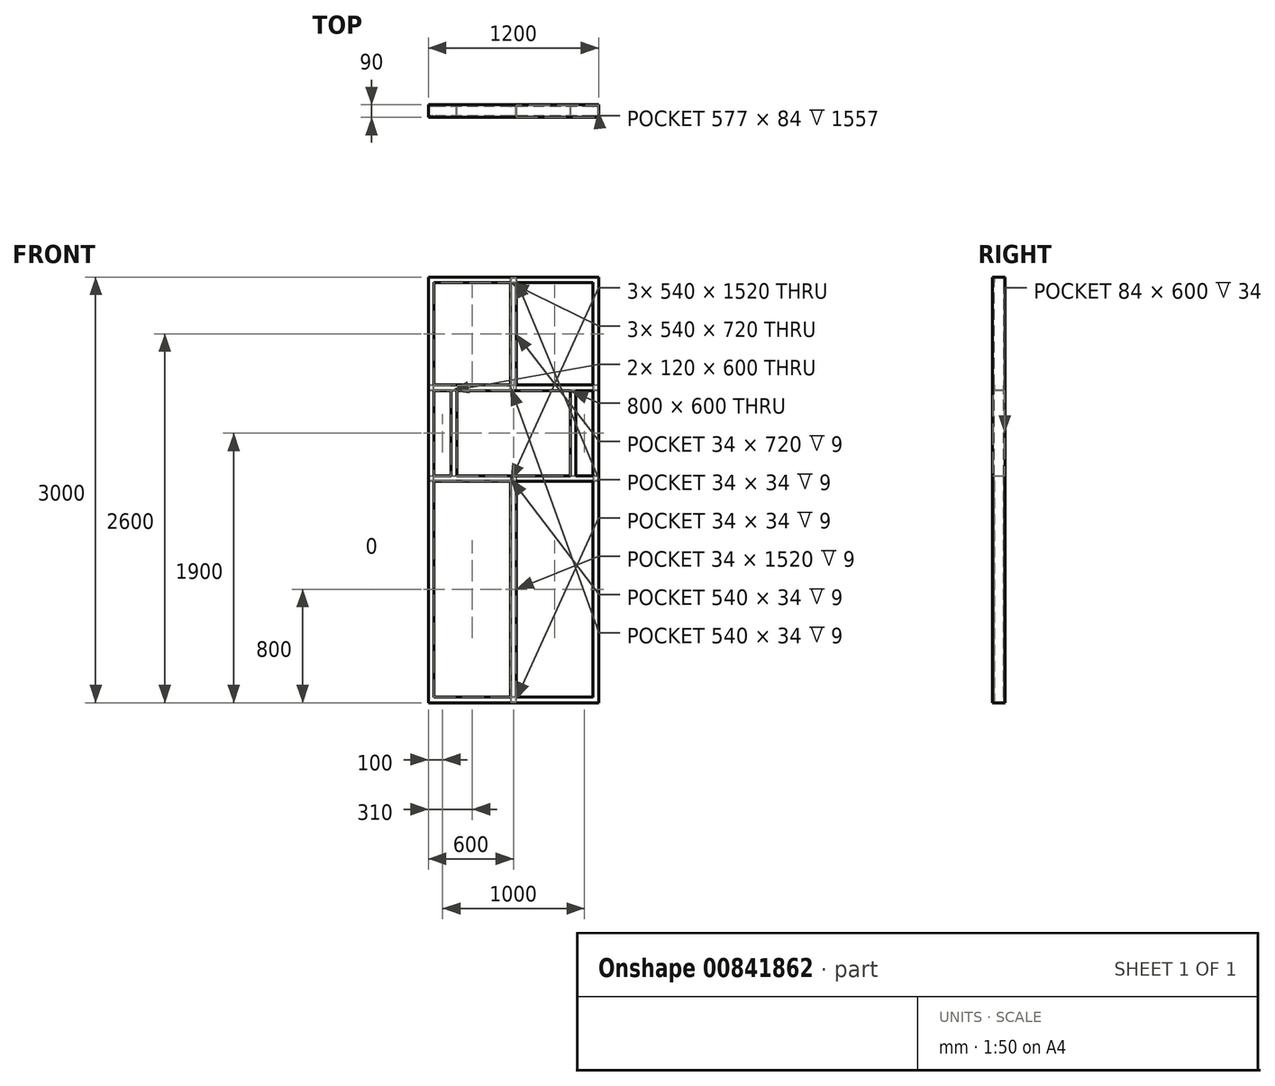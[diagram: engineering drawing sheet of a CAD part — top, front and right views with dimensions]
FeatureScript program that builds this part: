
annotation { "Feature Type Name" : "Feature", "Feature Type Description" : "" }
export const myFeature = defineFeature(function(context is Context, id is Id, definition is map)
    precondition{}
    {
        {
            var Q0;
            Q0=qCreatedBy(makeId("Front.planeOp"),FACE);
            var sketch = newSketch(context, id + "F0", { "sketchPlane" : qUnion([Q0])});
            skLineSegment(sketch, "E0.bottom", {"start": v(0, 0) * mm, "end": v(1200, 0) * mm});
            skLineSegment(sketch, "E0.top", {"start": v(0, 3000) * mm, "end": v(1200, 3000) * mm});
            skLineSegment(sketch, "E0.left", {"start": v(0, 0) * mm, "end": v(0, 3000) * mm});
            skLineSegment(sketch, "E0.right", {"start": v(1200, 0) * mm, "end": v(1200, 3000) * mm});
            skSolve(sketch);
        }
        {
            var Q0;
            Q0=qCreatedBy(makeId("Top.planeOp"),FACE);
            var sketch = newSketch(context, id + "F1", { "sketchPlane" : qUnion([Q0])});
            skLineSegment(sketch, "E1", {"start": v(0, 0) * mm, "end": v(0, -45) * mm});
            skLineSegment(sketch, "E2", {"start": v(0, -45) * mm, "end": v(40, -45) * mm});
            skLineSegment(sketch, "E3", {"start": v(40, -45) * mm, "end": v(40, -33) * mm});
            skLineSegment(sketch, "E4.MirrorCS", {"start": v(0, 0) * mm, "end": v(0, 45) * mm});
            skLineSegment(sketch, "E5.MirrorCS", {"start": v(0, 45) * mm, "end": v(40, 45) * mm});
            skLineSegment(sketch, "E6.MirrorCS", {"start": v(40, 45) * mm, "end": v(40, 33) * mm});
            skLineSegment(sketch, "E7.0", {"start": v(37, 42) * mm, "end": v(37, 33) * mm});
            skLineSegment(sketch, "E7.1", {"start": v(3, 42) * mm, "end": v(37, 42) * mm});
            skLineSegment(sketch, "E7.2", {"start": v(37, -42) * mm, "end": v(37, -33) * mm});
            skLineSegment(sketch, "E7.3", {"start": v(3, -42) * mm, "end": v(37, -42) * mm});
            skLineSegment(sketch, "E7.4", {"start": v(3, 0) * mm, "end": v(3, -42) * mm});
            skLineSegment(sketch, "E7.5", {"start": v(3, 0) * mm, "end": v(3, 42) * mm});
            skLineSegment(sketch, "E8", {"start": v(37, 33) * mm, "end": v(40, 33) * mm});
            skLineSegment(sketch, "E9", {"start": v(37, -33) * mm, "end": v(40, -33) * mm});
            skSolve(sketch);
        }
        {
            var Q0;
            Q0=qSketchRegion(id+"F1",true);
            var Q1;
            Q1=qConstructionFilter(qBodyType(qCreatedBy(id+"F0",EDGE),BodyType.WIRE),ConstructionObject.NO);
            sweep(context, id + "F2", {"profiles" : qUnion([Q0]), "path" : qUnion([Q1])});
        }
        {
            var Q0;
            Q0=qCreatedBy(makeId("Top.planeOp"),FACE);
            var sketch = newSketch(context, id + "F3", { "sketchPlane" : qUnion([Q0])});
            skLineSegment(sketch, "E10", {"start": v(580, -45) * mm, "end": v(620, -45) * mm});
            skLineSegment(sketch, "E11", {"start": v(620, -45) * mm, "end": v(620, 45) * mm});
            skLineSegment(sketch, "E12", {"start": v(620, 45) * mm, "end": v(580, 45) * mm});
            skLineSegment(sketch, "E13", {"start": v(580, 45) * mm, "end": v(580, 33) * mm});
            skLineSegment(sketch, "E14", {"start": v(580, -45) * mm, "end": v(580, -33) * mm});
            skLineSegment(sketch, "E15", {"start": v(900, -276.13) * mm, "end": v(900, 155.47) * mm, "construction": true});
            skLineSegment(sketch, "E16.0", {"start": v(1195, -40) * mm, "end": v(5, -40) * mm});
            skLineSegment(sketch, "E16.1", {"start": v(1195, 40) * mm, "end": v(1195, -40) * mm});
            skLineSegment(sketch, "E16.2", {"start": v(5, 40) * mm, "end": v(1195, 40) * mm});
            skLineSegment(sketch, "E16.3", {"start": v(5, 40) * mm, "end": v(5, -40) * mm});
            skLineSegment(sketch, "E17.0", {"start": v(583, 42) * mm, "end": v(583, 33) * mm});
            skLineSegment(sketch, "E17.1", {"start": v(583, -42) * mm, "end": v(583, -33) * mm});
            skLineSegment(sketch, "E17.2", {"start": v(583, -42) * mm, "end": v(617, -42) * mm});
            skLineSegment(sketch, "E17.3", {"start": v(617, -42) * mm, "end": v(617, 42) * mm});
            skLineSegment(sketch, "E17.4", {"start": v(617, 42) * mm, "end": v(583, 42) * mm});
            skLineSegment(sketch, "E18", {"start": v(583, -33) * mm, "end": v(580, -33) * mm});
            skLineSegment(sketch, "E19", {"start": v(583, 33) * mm, "end": v(580, 33) * mm});
            skSolve(sketch);
        }
        {
            var Q0;
            {var subQ1=sQuery(id+"F3.wireOp",EDGE,"E10");Q0=makeQuery(id+"F3.imprint","IMPRINT",FACE,{"disambiguationData":[TD([[makeQuery(id+"F3.imprint","IMPRINT",EDGE,{"derivedFrom":subQ1}),1.0]])]});}
            var Q1;
            {var subQ0=sQuery(id+"F3.wireOp",EDGE,"E16.0");var subQ1=sQuery(id+"F3.wireOp",EDGE,"E11");var subQ2=makeQuery(id+"F3.imprint","INTERSECT",VERTEX,{"derivedFrom":[subQ1,subQ0]});Q1=makeQuery(id+"F3.imprint","IMPRINT",FACE,{"disambiguationData":[TD([[makeQuery(id+"F3.imprint","IMPRINT",EDGE,{"disambiguationData":[TD([[subQ2,-1.0]])],"derivedFrom":subQ1}),1.0]])]});}
            var Q2;
            {var subQ0=sQuery(id+"F3.wireOp",EDGE,"E18");Q2=makeQuery(id+"F3.imprint","IMPRINT",FACE,{"disambiguationData":[TD([[makeQuery(id+"F3.imprint","IMPRINT",EDGE,{"derivedFrom":subQ0}),1.0]])]});}
            var Q3;
            {var subQ1=sQuery(id+"F3.wireOp",EDGE,"E12");Q3=makeQuery(id+"F3.imprint","IMPRINT",FACE,{"disambiguationData":[TD([[makeQuery(id+"F3.imprint","IMPRINT",EDGE,{"derivedFrom":subQ1}),1.0]])]});}
            var Q4;
            {var subQ0=sQuery(id+"F3.wireOp",EDGE,"E19");Q4=makeQuery(id+"F3.imprint","IMPRINT",FACE,{"disambiguationData":[TD([[makeQuery(id+"F3.imprint","IMPRINT",EDGE,{"derivedFrom":subQ0}),-1.0]])]});}
            var Q5;
            {var subQ0=sQuery(id+"F3.wireOp",EDGE,"fbeb7f0c-a459-400f-91ed-7fec257c8f050.MirrorCS");Q5=makeQuery(id+"F3.imprint","IMPRINT",FACE,{"disambiguationData":[TD([[makeQuery(id+"F3.imprint","IMPRINT",EDGE,{"derivedFrom":subQ0}),1.0]])]});}
            var Q6;
            {var subQ1=sQuery(id+"F3.wireOp",EDGE,"567eaf2c-da89-443f-b3b3-d68592a5250c0.MirrorCS");Q6=makeQuery(id+"F3.imprint","IMPRINT",FACE,{"disambiguationData":[TD([[makeQuery(id+"F3.imprint","IMPRINT",EDGE,{"derivedFrom":subQ1}),-1.0]])]});}
            var Q7;
            {var subQ0=sQuery(id+"F3.wireOp",EDGE,"E16.0");var subQ1=sQuery(id+"F3.wireOp",EDGE,"1e470031-5891-413e-a47c-f06d65b3e17f0.MirrorCS");var subQ2=makeQuery(id+"F3.imprint","INTERSECT",VERTEX,{"derivedFrom":[subQ1,subQ0]});Q7=makeQuery(id+"F3.imprint","IMPRINT",FACE,{"disambiguationData":[TD([[makeQuery(id+"F3.imprint","IMPRINT",EDGE,{"disambiguationData":[TD([[subQ2,-1.0]])],"derivedFrom":subQ1}),-1.0]])]});}
            var Q8;
            {var subQ5=sQuery(id+"F3.wireOp",EDGE,"ca9fbca5-8cf1-4a5b-8b27-837bc25230130.MirrorCS");Q8=makeQuery(id+"F3.imprint","IMPRINT",FACE,{"disambiguationData":[TD([[makeQuery(id+"F3.imprint","IMPRINT",EDGE,{"derivedFrom":subQ5}),-1.0]])]});}
            var Q9;
            {var subQ0=sQuery(id+"F3.wireOp",EDGE,"47aaed49-ff0d-4512-a623-d8c6419a6b470.MirrorCS");Q9=makeQuery(id+"F3.imprint","IMPRINT",FACE,{"disambiguationData":[TD([[makeQuery(id+"F3.imprint","IMPRINT",EDGE,{"derivedFrom":subQ0}),-1.0]])]});}
            var Q10;
            Q10=makeQuery(id+"F2.opSweep","SWEPT_FACE",FACE,{"disambiguationData":[OSD([sQuery(id+"F0.wireOp",EDGE,"E0.top"),sQuery(id+"F1.wireOp",EDGE,"E7.4"),sQuery(id+"F1.wireOp",EDGE,"E7.5")])]});
            extrude(context, id + "F4", {"entities" : qUnion([Q0, Q1, Q2, Q3, Q4, Q5, Q6, Q7, Q8, Q9]), "operationType" : NewBodyOperationType.ADD, "endBound" : BoundingType.UP_TO_SURFACE, "depth" : 25 * mm, "endBoundEntityFace" : qUnion([Q10]), "offsetDistance" : 25 * mm});
        }
        {
            var Q0;
            Q0=makeQuery(id+"F4.boolean.opBoolean","MERGE",FACE,{"derivedFrom":[makeQuery(id+"F2.opSweep","SWEPT_FACE",FACE,{"disambiguationData":[OSD([sQuery(id+"F0.wireOp",EDGE,"E0.left"),sQuery(id+"F1.wireOp",EDGE,"E2")])]}),makeQuery(id+"F4.opExtrude","SWEPT_FACE",FACE,{"disambiguationData":[OSD([sQuery(id+"F3.wireOp",EDGE,"E10")])]})]});
            var sketch = newSketch(context, id + "F5", { "sketchPlane" : qUnion([Q0])});
            skLineSegment(sketch, "E20.bottom", {"start": v(498.6, 2200) * mm, "end": v(696.59, 2200) * mm});
            skLineSegment(sketch, "E20.top", {"start": v(498.6, 1600) * mm, "end": v(696.59, 1600) * mm});
            skLineSegment(sketch, "E20.left", {"start": v(498.6, 2200) * mm, "end": v(498.6, 1600) * mm});
            skLineSegment(sketch, "E20.right", {"start": v(696.59, 2200) * mm, "end": v(696.59, 1600) * mm});
            skSolve(sketch);
        }
        {
            var Q0;
            Q0 = qSketchRegion(id + "F5", true);
            extrude(context, id + "F6", {"entities" : qUnion([Q0]), "operationType" : NewBodyOperationType.REMOVE, "endBound" : BoundingType.THROUGH_ALL, "oppositeDirection" : true, "depth" : 25 * mm, "offsetDistance" : 25 * mm});
        }
        {
            var Q0;
            Q0=makeQuery(id+"F6.boolean.opBoolean","SPLIT",FACE,{"disambiguationData":[TD([makeQuery(id+"F6.opExtrude","SWEPT_FACE",FACE,{"disambiguationData":[OSD([sQuery(id+"F5.wireOp",EDGE,"E20.top")])]})])],"derivedFrom":makeQuery(id+"F4.opExtrude","SWEPT_FACE",FACE,{"disambiguationData":[OSD([sQuery(id+"F3.wireOp",EDGE,"E11")])]})});
            var sketch = newSketch(context, id + "F7", { "sketchPlane" : qUnion([Q0])});
            skLineSegment(sketch, "E21", {"start": v(-45, 1600) * mm, "end": v(-45, 1560) * mm});
            skLineSegment(sketch, "E22", {"start": v(-45, 1600) * mm, "end": v(45, 1600) * mm});
            skLineSegment(sketch, "E23", {"start": v(45, 1600) * mm, "end": v(45, 1560) * mm});
            skLineSegment(sketch, "E24", {"start": v(45, 1560) * mm, "end": v(33, 1560) * mm});
            skLineSegment(sketch, "E25", {"start": v(-45, 1560) * mm, "end": v(-33, 1560) * mm});
            skLineSegment(sketch, "E26.0", {"start": v(-42, 1563) * mm, "end": v(-33, 1563) * mm});
            skLineSegment(sketch, "E26.1", {"start": v(42, 1563) * mm, "end": v(33, 1563) * mm});
            skLineSegment(sketch, "E26.2", {"start": v(42, 1597) * mm, "end": v(42, 1563) * mm});
            skLineSegment(sketch, "E26.3", {"start": v(-42, 1597) * mm, "end": v(42, 1597) * mm});
            skLineSegment(sketch, "E26.4", {"start": v(-42, 1597) * mm, "end": v(-42, 1563) * mm});
            skLineSegment(sketch, "E27", {"start": v(-33, 1563) * mm, "end": v(-33, 1560) * mm});
            skLineSegment(sketch, "E28", {"start": v(33, 1563) * mm, "end": v(33, 1560) * mm});
            skLineSegment(sketch, "E29", {"start": v(-204.7, 1900) * mm, "end": v(280.6, 1900) * mm, "construction": true});
            skLineSegment(sketch, "E30.MirrorCS", {"start": v(33, 2237) * mm, "end": v(33, 2240) * mm});
            skLineSegment(sketch, "E31.MirrorCS", {"start": v(-45, 2240) * mm, "end": v(-33, 2240) * mm});
            skLineSegment(sketch, "E32.MirrorCS", {"start": v(45, 2240) * mm, "end": v(33, 2240) * mm});
            skLineSegment(sketch, "E33.MirrorCS", {"start": v(42, 2237) * mm, "end": v(33, 2237) * mm});
            skLineSegment(sketch, "E34.MirrorCS", {"start": v(-42, 2237) * mm, "end": v(-33, 2237) * mm});
            skLineSegment(sketch, "E35.MirrorCS", {"start": v(-33, 2237) * mm, "end": v(-33, 2240) * mm});
            skLineSegment(sketch, "E36.MirrorCS", {"start": v(45, 2200) * mm, "end": v(45, 2240) * mm});
            skLineSegment(sketch, "E37.MirrorCS", {"start": v(42, 2203) * mm, "end": v(42, 2237) * mm});
            skLineSegment(sketch, "E38.MirrorCS", {"start": v(-45, 2200) * mm, "end": v(45, 2200) * mm});
            skLineSegment(sketch, "E39.MirrorCS", {"start": v(-45, 2200) * mm, "end": v(-45, 2240) * mm});
            skLineSegment(sketch, "E40.MirrorCS", {"start": v(-42, 2203) * mm, "end": v(-42, 2237) * mm});
            skLineSegment(sketch, "E41.MirrorCS", {"start": v(-42, 2203) * mm, "end": v(42, 2203) * mm});
            skSolve(sketch);
        }
        {
            var Q0;
            Q0=makeQuery(id+"F7.imprint","IMPRINT",FACE,{"disambiguationData":[TD([[makeQuery(id+"F7.imprint","IMPRINT",EDGE,{"derivedFrom":sQuery(id+"F7.wireOp",EDGE,"E30.MirrorCS")}),-1.0]])]});
            var Q1;
            Q1=makeQuery(id+"F7.imprint","IMPRINT",FACE,{"disambiguationData":[TD([[makeQuery(id+"F7.imprint","IMPRINT",EDGE,{"derivedFrom":sQuery(id+"F7.wireOp",EDGE,"E21")}),1.0]])]});
            var Q2;
            Q2=makeQuery(id+"F2.opSweep","SWEPT_FACE",FACE,{"disambiguationData":[OSD([sQuery(id+"F0.wireOp",EDGE,"E0.right"),sQuery(id+"F1.wireOp",EDGE,"E7.4"),sQuery(id+"F1.wireOp",EDGE,"E7.5")])]});
            var Q3;
            Q3=makeQuery(id+"F2.opSweep","SWEPT_FACE",FACE,{"disambiguationData":[OSD([sQuery(id+"F0.wireOp",EDGE,"E0.left"),sQuery(id+"F1.wireOp",EDGE,"E7.4"),sQuery(id+"F1.wireOp",EDGE,"E7.5")])]});
            extrude(context, id + "F8", {"entities" : qUnion([Q0, Q1]), "operationType" : NewBodyOperationType.ADD, "endBound" : BoundingType.UP_TO_SURFACE, "depth" : 25 * mm, "endBoundEntityFace" : qUnion([Q2]), "offsetDistance" : 25 * mm, "hasSecondDirection" : true, "secondDirectionBound" : SecondDirectionBoundingType.UP_TO_SURFACE, "secondDirectionOppositeDirection" : true, "secondDirectionDepth" : 25 * mm, "secondDirectionBoundEntityFace" : qUnion([Q3])});
        }
        {
            var Q0;
            Q0=makeQuery(id+"F8.boolean.opBoolean","MERGE",FACE,{"derivedFrom":[makeQuery(id+"F6.boolean.opBoolean","COPY",FACE,{"derivedFrom":makeQuery(id+"F6.opExtrude","SWEPT_FACE",FACE,{"disambiguationData":[OSD([sQuery(id+"F5.wireOp",EDGE,"E20.top")])]})}),makeQuery(id+"F8.opExtrude","SWEPT_FACE",FACE,{"disambiguationData":[OSD([sQuery(id+"F7.wireOp",EDGE,"E22")])]})]});
            var sketch = newSketch(context, id + "F9", { "sketchPlane" : qUnion([Q0])});
            skLineSegment(sketch, "E42", {"start": v(160, -45) * mm, "end": v(200, -45) * mm});
            skLineSegment(sketch, "E43", {"start": v(200, -45) * mm, "end": v(200, 45) * mm});
            skLineSegment(sketch, "E44", {"start": v(200, 45) * mm, "end": v(160, 45) * mm});
            skLineSegment(sketch, "E45", {"start": v(160, 45) * mm, "end": v(160, 33) * mm});
            skLineSegment(sketch, "E46", {"start": v(160, -45) * mm, "end": v(160, -33) * mm});
            skLineSegment(sketch, "E47.0", {"start": v(163, 42) * mm, "end": v(163, 33) * mm});
            skLineSegment(sketch, "E47.1", {"start": v(163, -42) * mm, "end": v(163, -33) * mm});
            skLineSegment(sketch, "E47.2", {"start": v(163, -42) * mm, "end": v(197, -42) * mm});
            skLineSegment(sketch, "E47.3", {"start": v(197, -42) * mm, "end": v(197, 42) * mm});
            skLineSegment(sketch, "E47.4", {"start": v(197, 42) * mm, "end": v(163, 42) * mm});
            skLineSegment(sketch, "E48", {"start": v(160, 33) * mm, "end": v(163, 33) * mm});
            skLineSegment(sketch, "E49", {"start": v(163, -33) * mm, "end": v(160, -33) * mm});
            skLineSegment(sketch, "E50", {"start": v(600, 101.56) * mm, "end": v(600, -102.52) * mm, "construction": true});
            skLineSegment(sketch, "E51.MirrorCS", {"start": v(1040, 45) * mm, "end": v(1040, 33) * mm});
            skLineSegment(sketch, "E52.MirrorCS", {"start": v(1037, 42) * mm, "end": v(1037, 33) * mm});
            skLineSegment(sketch, "E53.MirrorCS", {"start": v(1040, 33) * mm, "end": v(1037, 33) * mm});
            skLineSegment(sketch, "E54.MirrorCS", {"start": v(1037, -33) * mm, "end": v(1040, -33) * mm});
            skLineSegment(sketch, "E55.MirrorCS", {"start": v(1037, -42) * mm, "end": v(1003, -42) * mm});
            skLineSegment(sketch, "E56.MirrorCS", {"start": v(1037, -42) * mm, "end": v(1037, -33) * mm});
            skLineSegment(sketch, "E57.MirrorCS", {"start": v(1040, -45) * mm, "end": v(1040, -33) * mm});
            skLineSegment(sketch, "E58.MirrorCS", {"start": v(1040, -45) * mm, "end": v(1000, -45) * mm});
            skLineSegment(sketch, "E59.MirrorCS", {"start": v(1000, -45) * mm, "end": v(1000, 45) * mm});
            skLineSegment(sketch, "E60.MirrorCS", {"start": v(1003, -42) * mm, "end": v(1003, 42) * mm});
            skLineSegment(sketch, "E61.MirrorCS", {"start": v(1003, 42) * mm, "end": v(1037, 42) * mm});
            skLineSegment(sketch, "E62.MirrorCS", {"start": v(1000, 45) * mm, "end": v(1040, 45) * mm});
            skSolve(sketch);
        }
        {
            var Q0;
            Q0=makeQuery(id+"F9.imprint","IMPRINT",FACE,{"disambiguationData":[TD([[makeQuery(id+"F9.imprint","IMPRINT",EDGE,{"derivedFrom":sQuery(id+"F9.wireOp",EDGE,"E42")}),1.0]])]});
            var Q1;
            Q1=makeQuery(id+"F9.imprint","IMPRINT",FACE,{"disambiguationData":[TD([[makeQuery(id+"F9.imprint","IMPRINT",EDGE,{"derivedFrom":sQuery(id+"F9.wireOp",EDGE,"E51.MirrorCS")}),-1.0]])]});
            var Q2;
            Q2=makeQuery(id+"F8.boolean.opBoolean","MERGE",FACE,{"derivedFrom":[makeQuery(id+"F6.boolean.opBoolean","COPY",FACE,{"derivedFrom":makeQuery(id+"F6.opExtrude","SWEPT_FACE",FACE,{"disambiguationData":[OSD([sQuery(id+"F5.wireOp",EDGE,"E20.bottom")])]})}),makeQuery(id+"F8.opExtrude","SWEPT_FACE",FACE,{"disambiguationData":[OSD([sQuery(id+"F7.wireOp",EDGE,"E38.MirrorCS")])]})]});
            extrude(context, id + "F10", {"entities" : qUnion([Q0, Q1]), "operationType" : NewBodyOperationType.ADD, "endBound" : BoundingType.UP_TO_SURFACE, "depth" : 25 * mm, "endBoundEntityFace" : qUnion([Q2]), "offsetDistance" : 25 * mm});
        }
    });
